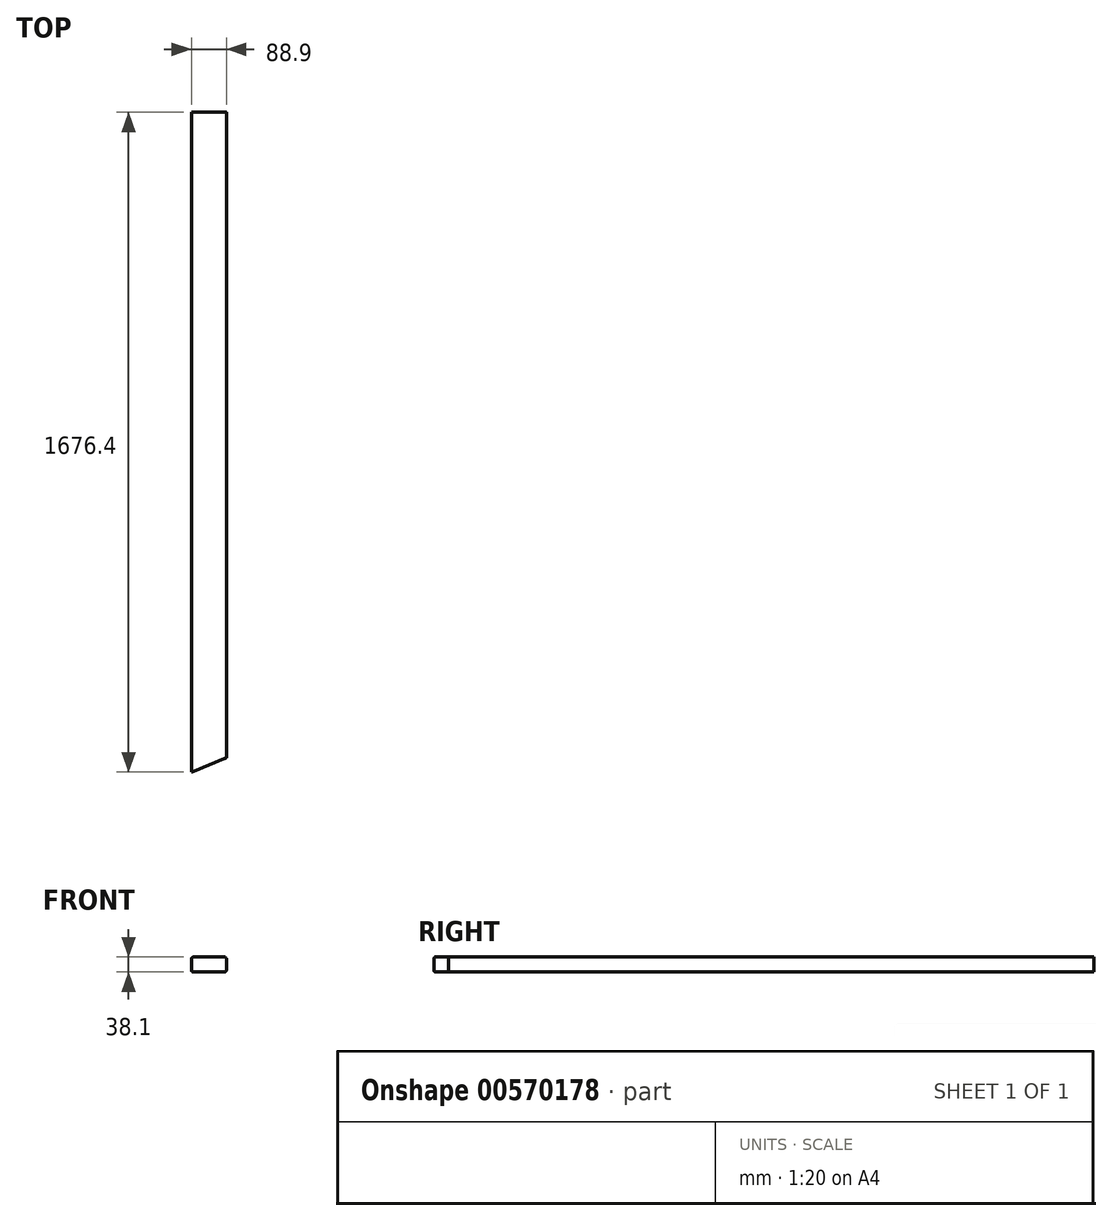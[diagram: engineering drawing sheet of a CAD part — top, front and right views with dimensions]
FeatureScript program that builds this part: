
annotation { "Feature Type Name" : "Feature", "Feature Type Description" : "" }
export const myFeature = defineFeature(function(context is Context, id is Id, definition is map)
    precondition{}
    {
        {
            var Q0;
            Q0=qCreatedBy(makeId("Front.planeOp"),FACE);
            var sketch = newSketch(context, id + "F0", { "sketchPlane" : qUnion([Q0])});
            skLineSegment(sketch, "E0.bottom", {"start": v(0, 0) * mm, "end": v(88.9, 0) * mm});
            skLineSegment(sketch, "E0.top", {"start": v(0, 38.1) * mm, "end": v(88.9, 38.1) * mm});
            skLineSegment(sketch, "E0.left", {"start": v(0, 0) * mm, "end": v(0, 38.1) * mm});
            skLineSegment(sketch, "E0.right", {"start": v(88.9, 0) * mm, "end": v(88.9, 38.1) * mm});
            skSolve(sketch);
        }
        {
            var Q0;
            Q0 = qSketchRegion(id + "F0", true);
            extrude(context, id + "F1", {"entities" : qUnion([Q0]), "depth" : 1676.4 * mm, "offsetDistance" : 25.4 * mm});
        }
        {
            var Q0;
            Q0=makeQuery(id+"F1.opExtrude","SWEPT_FACE",FACE,{"disambiguationData":[OSD([sQuery(id+"F0.wireOp",EDGE,"E0.top")])]});
            var sketch = newSketch(context, id + "F2", { "sketchPlane" : qUnion([Q0])});
            skLineSegment(sketch, "E1", {"start": v(0, -1676.4) * mm, "end": v(88.9, -1676.4) * mm});
            skLineSegment(sketch, "E2", {"start": v(88.9, -1676.4) * mm, "end": v(88.9, -1640.12) * mm});
            skLineSegment(sketch, "E3", {"start": v(88.9, -1640.12) * mm, "end": v(0, -1676.4) * mm});
            skSolve(sketch);
        }
        {
            var Q0;
            Q0=makeQuery(id+"F2.imprint","IMPRINT",FACE,{"disambiguationData":[TD([[makeQuery(id+"F2.imprint","IMPRINT",EDGE,{"derivedFrom":sQuery(id+"F2.wireOp",EDGE,"E1")}),1.0]])]});
            extrude(context, id + "F3", {"entities" : qUnion([Q0]), "operationType" : NewBodyOperationType.REMOVE, "oppositeDirection" : true, "depth" : 84.07 * mm, "offsetDistance" : 25.4 * mm});
        }
        {
            var Q0;
            Q0=makeQuery(id+"F1.opExtrude","SWEPT_EDGE",EDGE,{"disambiguationData":[OSD([sQuery(id+"F0.wireOp",EDGE,"E0.top"),sQuery(id+"F0.wireOp",EDGE,"E0.left")])]});
            var Q1;
            Q1=makeQuery(id+"F1.opExtrude","SWEPT_EDGE",EDGE,{"disambiguationData":[OSD([sQuery(id+"F0.wireOp",EDGE,"E0.top"),sQuery(id+"F0.wireOp",EDGE,"E0.right")])]});
            var Q2;
            Q2=makeQuery(id+"F1.opExtrude","SWEPT_EDGE",EDGE,{"disambiguationData":[OSD([sQuery(id+"F0.wireOp",EDGE,"E0.bottom"),sQuery(id+"F0.wireOp",EDGE,"E0.left")])]});
            var Q3;
            Q3=makeQuery(id+"F1.opExtrude","SWEPT_EDGE",EDGE,{"disambiguationData":[OSD([sQuery(id+"F0.wireOp",EDGE,"E0.bottom"),sQuery(id+"F0.wireOp",EDGE,"E0.right")])]});
            fillet(context, id + "F4", {"entities" : qUnion([Q0, Q1, Q2, Q3]), "radius" : 5.08 * mm, "tangentPropagation" : true, "allowEdgeOverflow" : false});
        }
    });
